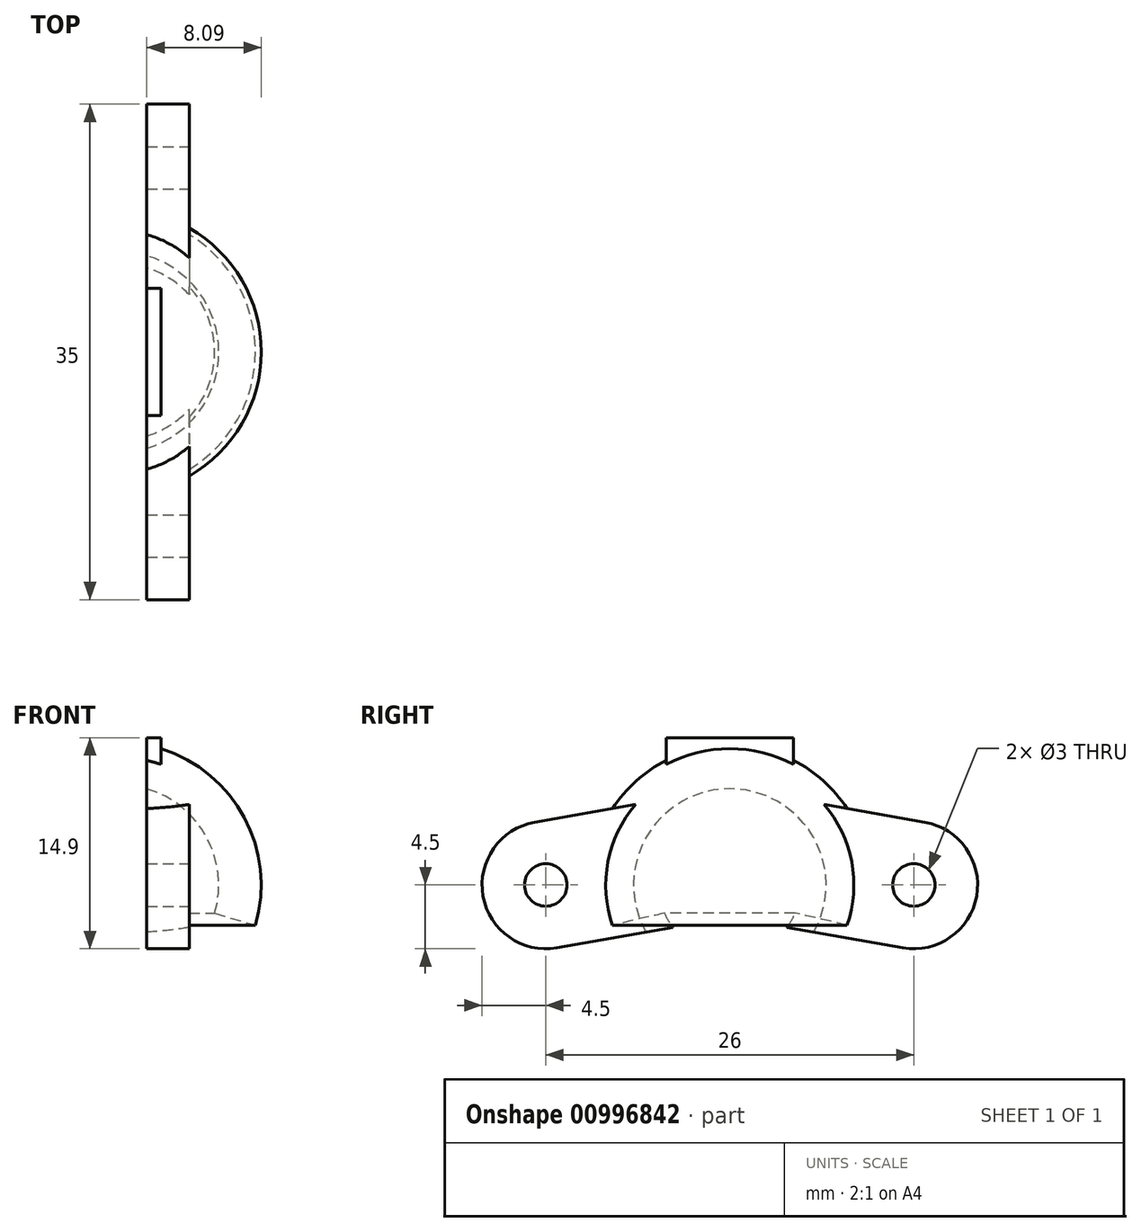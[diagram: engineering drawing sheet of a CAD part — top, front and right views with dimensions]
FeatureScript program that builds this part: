
annotation { "Feature Type Name" : "Feature", "Feature Type Description" : "" }
export const myFeature = defineFeature(function(context is Context, id is Id, definition is map)
    precondition{}
    {
        {
            var Q0;
            Q0=qCreatedBy(makeId("Front.planeOp"),FACE);
            var sketch = newSketch(context, id + "F0", { "sketchPlane" : qUnion([Q0])});
            skLineSegment(sketch, "E0", {"start": v(0, 0) * mm, "end": v(0, 35.27) * mm, "construction": true});
            skArc(sketch, "E1", {"start": v(6.8, 0) * mm, "mid": v(5.68, 6.25) * mm, "end": v(0, 9.09) * mm});
            skArc(sketch, "E2.0", {"start": v(9.68, -0.85) * mm, "mid": v(8.08, 8.04) * mm, "end": v(0, 12.09) * mm});
            skLineSegment(sketch, "E3", {"start": v(0, 9.09) * mm, "end": v(0, 12.09) * mm});
            skLineSegment(sketch, "E4", {"start": v(6.8, 0) * mm, "end": v(9.68, -0.85) * mm});
            skSolve(sketch);
        }
        {
            var Q0;
            Q0 = qSketchRegion(id + "F0", true);
            var Q1;
            Q1=sQuery(id+"F0.wireOp",EDGE,"E0");
            revolve(context, id + "F1", {"surfaceOperationType" : NewSurfaceOperationType.NEW, "entities" : qUnion([Q0]), "axis" : qUnion([Q1]), "revolveType" : RevolveType.FULL});
        }
        {
            var Q0;
            Q0=qCreatedBy(makeId("Right.planeOp"),FACE);
            var sketch = newSketch(context, id + "F2", { "sketchPlane" : qUnion([Q0])});
            skCircle(sketch, "E5", {"center": v(0, 30) * mm, "radius": 1.5 * mm});
            skArc(sketch, "E6", {"start": v(4.5, 30) * mm, "mid": v(0, 34.5) * mm, "end": v(-4.5, 30) * mm});
            skLineSegment(sketch, "E7", {"start": v(-4.5, 30) * mm, "end": v(-4.5, 25.5) * mm});
            skLineSegment(sketch, "E8", {"start": v(-4.5, 25.5) * mm, "end": v(4.5, 25.5) * mm});
            skLineSegment(sketch, "E9", {"start": v(4.5, 25.5) * mm, "end": v(4.5, 30) * mm});
            skSolve(sketch);
        }
        {
            var Q0;
            Q0 = qSketchRegion(id + "F2", true);
            extrude(context, id + "F3", {"entities" : qUnion([Q0]), "endBound" : BoundingType.SYMMETRIC, "depth" : 6 * mm, "offsetDistance" : 25 * mm});
        }
        {
            var Q0;
            Q0=makeQuery(id+"F3.opExtrude","SWEPT_FACE",FACE,{"disambiguationData":[OSD([sQuery(id+"F2.wireOp",EDGE,"E8")])]});
            extrude(context, id + "F4", {"entities" : qUnion([Q0]), "operationType" : NewBodyOperationType.ADD, "endBound" : BoundingType.UP_TO_NEXT, "depth" : 25 * mm, "offsetDistance" : 25 * mm});
        }
        {
            var Q0;
            Q0=qCreatedBy(makeId("Right.planeOp"),FACE);
            var sketch = newSketch(context, id + "F5", { "sketchPlane" : qUnion([Q0])});
            skLineSegment(sketch, "E10", {"start": v(13, 2) * mm, "end": v(0, 2) * mm, "construction": true});
            skCircle(sketch, "E11", {"center": v(13, 2) * mm, "radius": 1.5 * mm});
            skArc(sketch, "E12.0", {"start": v(12.22, -2.43) * mm, "mid": v(17.43, 1.22) * mm, "end": v(13.78, 6.43) * mm});
            skLineSegment(sketch, "E13", {"start": v(12.22, -2.43) * mm, "end": v(-1.56, 0) * mm});
            skLineSegment(sketch, "E14", {"start": v(-1.56, 0) * mm, "end": v(0, 8.86) * mm});
            skLineSegment(sketch, "E15", {"start": v(0, 8.86) * mm, "end": v(13.78, 6.43) * mm});
            skSolve(sketch);
        }
        {
            var Q0;
            Q0 = qSketchRegion(id + "F5", true);
            extrude(context, id + "F6", {"entities" : qUnion([Q0]), "oppositeDirection" : true, "depth" : 1 * mm, "offsetDistance" : 25 * mm, "hasSecondDirection" : true, "secondDirectionOppositeDirection" : false, "secondDirectionDepth" : 5 * mm});
        }
        {
            var Q0;
            Q0=makeQuery(id+"F6.opExtrude","SWEPT_BODY",BODY,{"disambiguationData":[OSD([sQuery(id+"F5.wireOp",EDGE,"E11"),sQuery(id+"F5.wireOp",EDGE,"E12.0"),sQuery(id+"F5.wireOp",EDGE,"E13"),sQuery(id+"F5.wireOp",EDGE,"E14"),sQuery(id+"F5.wireOp",EDGE,"E15")])]});
            var Q1;
            Q1=qCreatedBy(makeId("Front.planeOp"),FACE);
            mirror(context, id + "F7", {"operationType" : NewBodyOperationType.ADD, "entities" : qUnion([Q0]), "mirrorPlane" : qUnion([Q1])});
        }
        {
            var Q0;
            Q0=qCreatedBy(makeId("Front.planeOp"),FACE);
            var sketch = newSketch(context, id + "F8", { "sketchPlane" : qUnion([Q0])});
            skLineSegment(sketch, "E16", {"start": v(0, 0) * mm, "end": v(0, 17.38) * mm, "construction": true});
            skArc(sketch, "E17", {"start": v(0, -5.09) * mm, "mid": v(7.09, 2) * mm, "end": v(0, 9.09) * mm});
            skLineSegment(sketch, "E18", {"start": v(0, 9.09) * mm, "end": v(0, -5.09) * mm});
            skSolve(sketch);
        }
        {
            var Q0;
            Q0 = qSketchRegion(id + "F8", true);
            var Q1;
            Q1=sQuery(id+"F8.wireOp",EDGE,"E16");
            revolve(context, id + "F9", {"operationType" : NewBodyOperationType.REMOVE, "surfaceOperationType" : NewSurfaceOperationType.NEW, "entities" : qUnion([Q0]), "axis" : qUnion([Q1]), "revolveType" : RevolveType.FULL, "oppositeDirection" : true});
        }
        {
            var Q0;
            {var subQ0=sQuery(id+"F5.wireOp",EDGE,"E11");var subQ1=sQuery(id+"F5.wireOp",EDGE,"E12.0");var subQ2=sQuery(id+"F5.wireOp",EDGE,"E13");var subQ3=sQuery(id+"F5.wireOp",EDGE,"E15");var subQ4=makeQuery(id+"F6.opExtrude","CAP_FACE",FACE,{"disambiguationData":[OSD([subQ0,subQ1,subQ2,sQuery(id+"F5.wireOp",EDGE,"E14"),subQ3])],"isStart":true});Q0=makeQuery(id+"F9.boolean.opBoolean","SPLIT",FACE,{"disambiguationData":[TD([makeQuery(id+"F7.opPattern","COPY",FACE,{"derivedFrom":makeQuery(id+"F6.opExtrude","SWEPT_FACE",FACE,{"disambiguationData":[OSD([subQ0])]}),"instanceName":"1"})])],"derivedFrom":makeQuery(id+"F7.boolean.opBoolean","MERGE",FACE,{"derivedFrom":[subQ4,makeQuery(id+"F7.opPattern","COPY",FACE,{"derivedFrom":subQ4,"instanceName":"1"})]})});}
            var Q1;
            {var subQ0=sQuery(id+"F5.wireOp",EDGE,"E11");var subQ1=sQuery(id+"F5.wireOp",EDGE,"E12.0");var subQ2=sQuery(id+"F5.wireOp",EDGE,"E13");var subQ3=sQuery(id+"F5.wireOp",EDGE,"E15");var subQ4=makeQuery(id+"F6.opExtrude","CAP_FACE",FACE,{"disambiguationData":[OSD([subQ0,subQ1,subQ2,sQuery(id+"F5.wireOp",EDGE,"E14"),subQ3])],"isStart":false});Q1=makeQuery(id+"F9.boolean.opBoolean","SPLIT",FACE,{"disambiguationData":[TD([makeQuery(id+"F7.opPattern","COPY",FACE,{"derivedFrom":makeQuery(id+"F6.opExtrude","SWEPT_FACE",FACE,{"disambiguationData":[OSD([subQ0])]}),"instanceName":"1"})])],"derivedFrom":makeQuery(id+"F7.boolean.opBoolean","MERGE",FACE,{"derivedFrom":[subQ4,makeQuery(id+"F7.opPattern","COPY",FACE,{"derivedFrom":subQ4,"instanceName":"1"})]})});}
            cPlane(context, id + "F10", {"entities" : qUnion([Q0, Q1]), "cplaneType" : CPlaneType.MID_PLANE, "offset" : 25 * mm, "width" : 150 * mm, "height" : 150 * mm});
        }
        {
            var Q0;
            Q0=qCreatedBy(id+"F10.planeOp",FACE);
            var sketch = newSketch(context, id + "F11", { "sketchPlane" : qUnion([Q0])});
            skLineSegment(sketch, "E19.bottom", {"start": v(-17.5, 12.4) * mm, "end": v(17.5, 12.4) * mm});
            skLineSegment(sketch, "E19.top", {"start": v(-17.5, -2.5) * mm, "end": v(17.5, -2.5) * mm});
            skLineSegment(sketch, "E19.left", {"start": v(-17.5, 12.4) * mm, "end": v(-17.5, -2.5) * mm});
            skLineSegment(sketch, "E19.right", {"start": v(17.5, 12.4) * mm, "end": v(17.5, -2.5) * mm});
            skLineSegment(sketch, "E20", {"start": v(0, 12.4) * mm, "end": v(0, 0) * mm, "construction": true});
            skSolve(sketch);
        }
        {
            var Q0;
            Q0 = qSketchRegion(id + "F11", true);
            extrude(context, id + "F12", {"entities" : qUnion([Q0]), "operationType" : NewBodyOperationType.INTERSECT, "depth" : 25 * mm, "offsetDistance" : 25 * mm});
        }
    });
